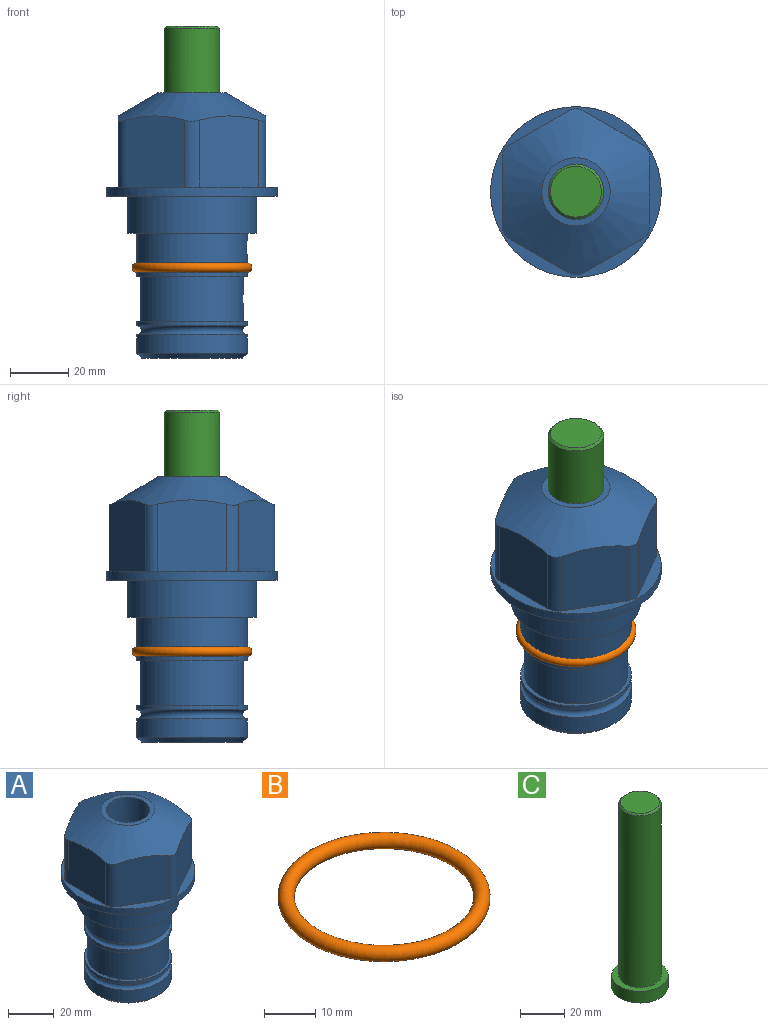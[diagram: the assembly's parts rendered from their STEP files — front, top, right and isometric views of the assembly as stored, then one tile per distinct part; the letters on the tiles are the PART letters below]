
ASSEMBLY  parts=3 mates=1
PART A: 36 faces, bbox 58.7x58.7x91.2 mm
  f0: cylinder r=17.78mm len=35.56mm, axis (0,0,1), area 1670.8mm2, adj f23,f24,f31
  f1: cylinder r=19.05mm len=38.1mm, axis (0,0,1), area 1191.9mm2, adj f26,f27,f30
  f2: plane 58.66x58.66mm, normal (0,0,-1), area 1150.6mm2, adj f3,f28
  f3: cylinder r=29.33mm len=58.66mm, axis (0,0,-1), area 585.1mm2, adj f2,f4
  f4: plane 58.66x58.66mm, normal (0,0,1), area 475.9mm2, adj f3,f5,f6,f7,f8,f9,f10,f11
  f5: plane 24.5x20.32mm, normal (-0.5,0.87,0), area 562.8mm2, adj f4,f15,f16,f17
  f6: plane 24.5x20.32mm, normal (0.5,0.87,0), area 562.8mm2, adj f4,f14,f15,f17
  f7: plane 24.5x23.48mm, normal (1,0,0), area 562.8mm2, adj f4,f13,f14,f17
  f8: plane 24.5x20.32mm, normal (0.5,-0.87,0), area 562.8mm2, adj f4,f12,f13,f17
  f9: plane 24.5x20.32mm, normal (-0.5,-0.87,0), area 562.8mm2, adj f4,f11,f12,f17
  f10: plane 24.5x23.48mm, normal (-1,0,0), area 562.8mm2, adj f4,f11,f16,f17
  f11: cylinder r=5.08mm len=23.01mm, axis (0,0,-1), area 121.2mm2, adj f4,f9,f10,f17
  f12: cylinder r=5.08mm len=23.01mm, axis (0,0,-1), area 121.2mm2, adj f4,f8,f9,f17
  f13: cylinder r=5.08mm len=23.01mm, axis (0,0,-1), area 121.2mm2, adj f4,f7,f8,f17
  f14: cylinder r=5.08mm len=23.01mm, axis (0,0,-1), area 121.2mm2, adj f4,f6,f7,f17
  f15: cylinder r=5.08mm len=23.01mm, axis (0,0,-1), area 121.2mm2, adj f4,f5,f6,f17
  f16: cylinder r=5.08mm len=23.01mm, axis (0,0,-1), area 121.2mm2, adj f4,f5,f10,f17
  f17: cone r=11.73mm half-angle=60deg, axis (0,0,-1), area 2071.8mm2, adj f5,f6,f7,f8,f9,f10,f11,f12
  f18: plane 23.46x23.46mm, normal (0,0,1), area 147.4mm2, adj f17,f35
  f19: plane 34.93x34.93mm, normal (0,0,-1), area 958mm2, adj f29
  f20: cylinder r=19.05mm len=38.1mm, axis (0,0,1), area 760.1mm2, adj f21,f29
  f21: torus R=19.05mm, axis (0,0,1), area 565.3mm2, adj f20,f22
  f22: cylinder r=19.05mm len=38.1mm, axis (0,0,1), area 190mm2, adj f21,f23
  f23: plane 38.1x38.1mm, normal (0,0,1), area 146.9mm2, adj f0,f22
  f24: plane 38.1x38.1mm, normal (0,0,-1), area 146.9mm2, adj f0,f25
  f25: cylinder r=19.05mm len=38.1mm, axis (0,0,1), area 190mm2, adj f24,f26
  f26: torus R=19.05mm, axis (0,0,1), area 565.3mm2, adj f1,f25
  f27: plane 44.45x44.45mm, normal (0,0,-1), area 411.7mm2, adj f1,f28
  f28: cylinder r=22.23mm len=44.45mm, axis (0,0,1), area 1773.5mm2, adj f2,f27
  f29: cone r=19.05mm half-angle=45deg, axis (0,0,1), area 257.5mm2, adj f19,f20
  f30: cylinder r=3.17mm len=6.75mm, axis (-1,0,0), area 128mm2, adj f1,f33
  f31: cylinder r=3.17mm len=6.35mm, axis (-1,0,0), area 102.5mm2, adj f0,f33
  f32: plane 25.4x25.4mm, normal (0,0,1), area 506.7mm2, adj f33
  f33: cylinder r=12.7mm len=66.42mm, axis (0,0,-1), area 5236.2mm2, adj f30,f31,f32,f34
  f34: cone r=9.53mm half-angle=30deg, axis (0,0,-1), area 443.4mm2, adj f33,f35
  f35: cylinder r=9.53mm len=19.05mm, axis (0,0,-1), area 849mm2, adj f18,f34
PART B: 1 faces, bbox 44.7x44.7x3.2 mm
  f0: torus R=19.05mm, axis (0,0,1), area 1193.9mm2
PART C: 6 faces, bbox 25.4x25.4x101.6 mm
  f0: plane 17.46x17.46mm, normal (0,0,1), area 239.5mm2, adj f5
  f1: plane 25.4x25.4mm, normal (0,0,-1), area 506.7mm2, adj f2
  f2: cylinder r=12.7mm len=25.4mm, axis (0,0,1), area 506.7mm2, adj f1,f3
  f3: plane 25.4x25.4mm, normal (0,0,1), area 221.7mm2, adj f2,f4
  f4: cylinder r=9.53mm len=94.46mm, axis (0,0,1), area 5653mm2, adj f3,f5
  f5: cone r=8.73mm half-angle=45deg, axis (0,0,-1), area 64.4mm2, adj f0,f4
PLACE A at identity fixed
PLACE B at identity
PLACE C t=(0,0,-15.08)mm
MATE cylindrical C.f2 <-> A.f0  axis (0,0,1) through (0,0,10.56)mm
